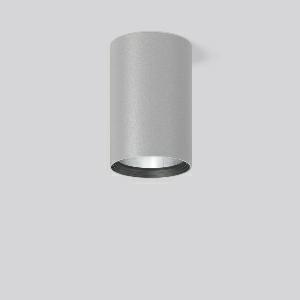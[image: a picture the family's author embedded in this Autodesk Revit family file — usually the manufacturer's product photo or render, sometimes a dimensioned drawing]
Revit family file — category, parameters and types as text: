
# Revit family: heledon_maxi_a_931226_004_2_fad0
name_source: partatom
category: Lighting Fixtures
units: mm (PartAtom-declared; Revit-internal decimal feet)

## family parameters
Cut with Voids When Loaded = No
Host = Face
Light Source = No
Part Type = Normal
Room Calculation Point = No
Round Connector Dimension = Use Diameter
Shared = No

## types (1)
- HELEDON maxi A (1 x LED Modul 927, 3950 lm, 2700)
    Apparent Load = 35 VA
    Approval mark = CE
    CIE Flux Codes = 97 100 100 100 100
    Color Rendering = 92
    Color Temperature = 2700
    Default Elevation = 1800 mm
    Description = Series: HELEDON maxi
Cylindrical surface-mounted downlight. Housing: die-cast aluminium, powder-coated. Internal ceiling frame polycarbonate with bayonet mounting. Black plastic ring and recessed LED to prevent glare from the side. Optical assembly with reflector made of MIRO-Silver with 98% total light reflection for outstanding efficiency - can be changed without tools. Best colour rendering index Ra>90. Suitable for Ceiling mounting. Easy installation with a separate ceiling frame with bayonet mounting and plug connection. Driver integrated. Connected via plug-in connector. High quality converter without flickering and stroboscopic effect. The following accessories can be mounted without use of tools: interchangeable lenses, decorative glasses, honeycomb louvre, clear and frosted diffusers, white interchangeable plastic ring. 
Colour: silver
Diameter: 123 mm
Height: 183 mm
Lamp: LED
Socket: without socket
Colour temperature: 2700K
Colour rendering index (CRI): 92
System power: 35 W
Rated luminous flux: 3950 lm
Luminous efficiency: 113 lm/W
Control gear: Regulated power supply
Protection class: I
Type of protection: IP 20
    Height = 183 mm
    Lamp = 1 x LED Modul 927
    Lamp Light Flux = 3950 lm
    Lamp count = 1
    Length = 123 mm
    Lifetime = 50000 h
    Luminous efficacy = 113 lm/W
    Manufacturer = RZB
    ModVariant = No
    Model = 931226.004.2
    Mounting Place = Ceiling
    Mounting Type = Surface mounted
    Number of Poles = 1
    OnlyDefault = Yes
    Power Factor = 1
    Product Name = HELEDON maxi A
    Product group = Surface mounted downlights
    ProductGroupID = 302
    Protection Class = Protection class I
    Protection Degree = IP 20
    RLX_Detail_Level = 1
    RLX_Emergency_Light_Flux = 0 lm
    RLX_Emergency_Type = 0
    RLX_Emergency_Type_DB = No
    RlxData = <blob elided: 98701 chars, md5=bb88bc39>
    Socket = socket
    Standby Power = 0 W
    System Light Flux = 3950 lm
    System Power = 35 W
    Type Comments = Product without accessories
    Type Image = 931192.004.jpg
    URL = http://relux.com
    VarID = ---
    Voltage = 230 V
    Voltage Range = 220-240 V
    Weight = 0.00 kg
    Width = 0 mm  [stored 0 ft]

note: [stored X ft] marks values corroborated as IEEE doubles in the binary element streams (Revit-internal decimal feet)

## geometry (parser evidence)
native form markers: Blend x4, Sweep x10
no freeform markers — native parametric forms only
